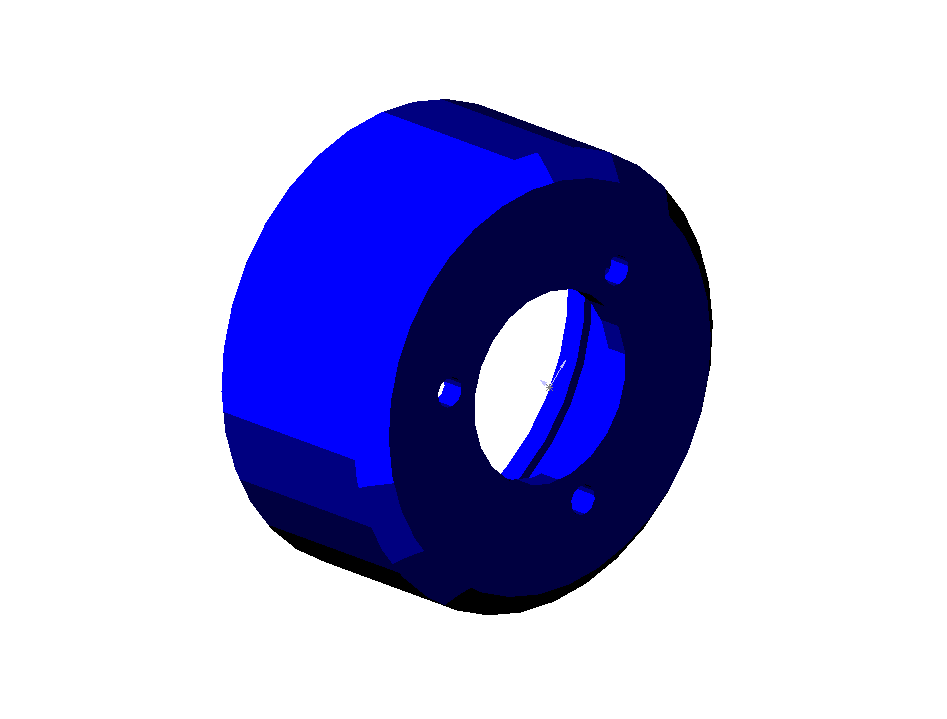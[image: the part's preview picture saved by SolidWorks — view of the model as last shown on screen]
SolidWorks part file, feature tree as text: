
SOLIDWORKS PART (.sldprt)
format: sldprt  version: not decoded by parser v0  size: 142,848 bytes
history: native  units: mm
features: sketch x9, cut_extrude x8, plane x4, chamfer x2, material x1, extrude x1, pattern_circular x1 (+10 scaffold rows collapsed)
feature tree (36):
  scaffold x10  (default folders/planes/origin — collapsed)
  material  "Matériau <non spécifié>"
  plane  "Plan1"
  plane  "Plan2"
  plane  "Plan3"
  sketch  "Esquisse1"  dims[D1=38.0mm]
  extrude  "Base-Extrusion"  Depth=18mm
  sketch  "Esquisse2"  dims[D1=26.0mm]
  cut_extrude  "Enlèv. mat.-Extru.1"  Depth=4mm
  sketch  "Esquisse3"  dims[D1=16.0mm]
  cut_extrude  "Enlèv. mat.-Extru.2"  [1 undecoded]
  sketch  "Esquisse4"  dims[D1=2.5mm D2=10.75mm]
  cut_extrude  "Enlèv. mat.-Extru.3"  [1 undecoded]
  pattern_circular  "Répétition circulaire1"  Count=3 Angle=120deg
  sketch  "Esquisse5"  dims[D1=26.0mm]
  cut_extrude  "Enlèv. mat.-Extru.4"  Depth=2mm
  sketch  "Esquisse6"  dims[D1=36.5mm]
  cut_extrude  "Enlèv. mat.-Extru.5"  Depth=1mm
  plane  "Plan4"  Offset=8mm
  sketch  "Esquisse7"  dims[D1=34.0mm]
  cut_extrude  "Enlèv. mat.-Extru.6"  [1 undecoded]
  sketch  "Esquisse8"  dims[D1=34.37mm]
  cut_extrude  "Enlèv. mat.-Extru.7"  Depth=4mm
  sketch  "Esquisse9"
  cut_extrude  "Enlèv. mat.-Extru.8"  Depth=1mm
  chamfer  "Chanfrein1"  Distance=2mm Angle=45deg
  chamfer  "Chanfrein2"  Distance=0.5mm Angle=45deg
decode coverage: 17 of 21 modeling features carry decoded parameters
note: 3 parameter values undecoded
summary: no parameter record found for 3 features
note: suppression state not decoded; provenance and decode notes live in map.json
